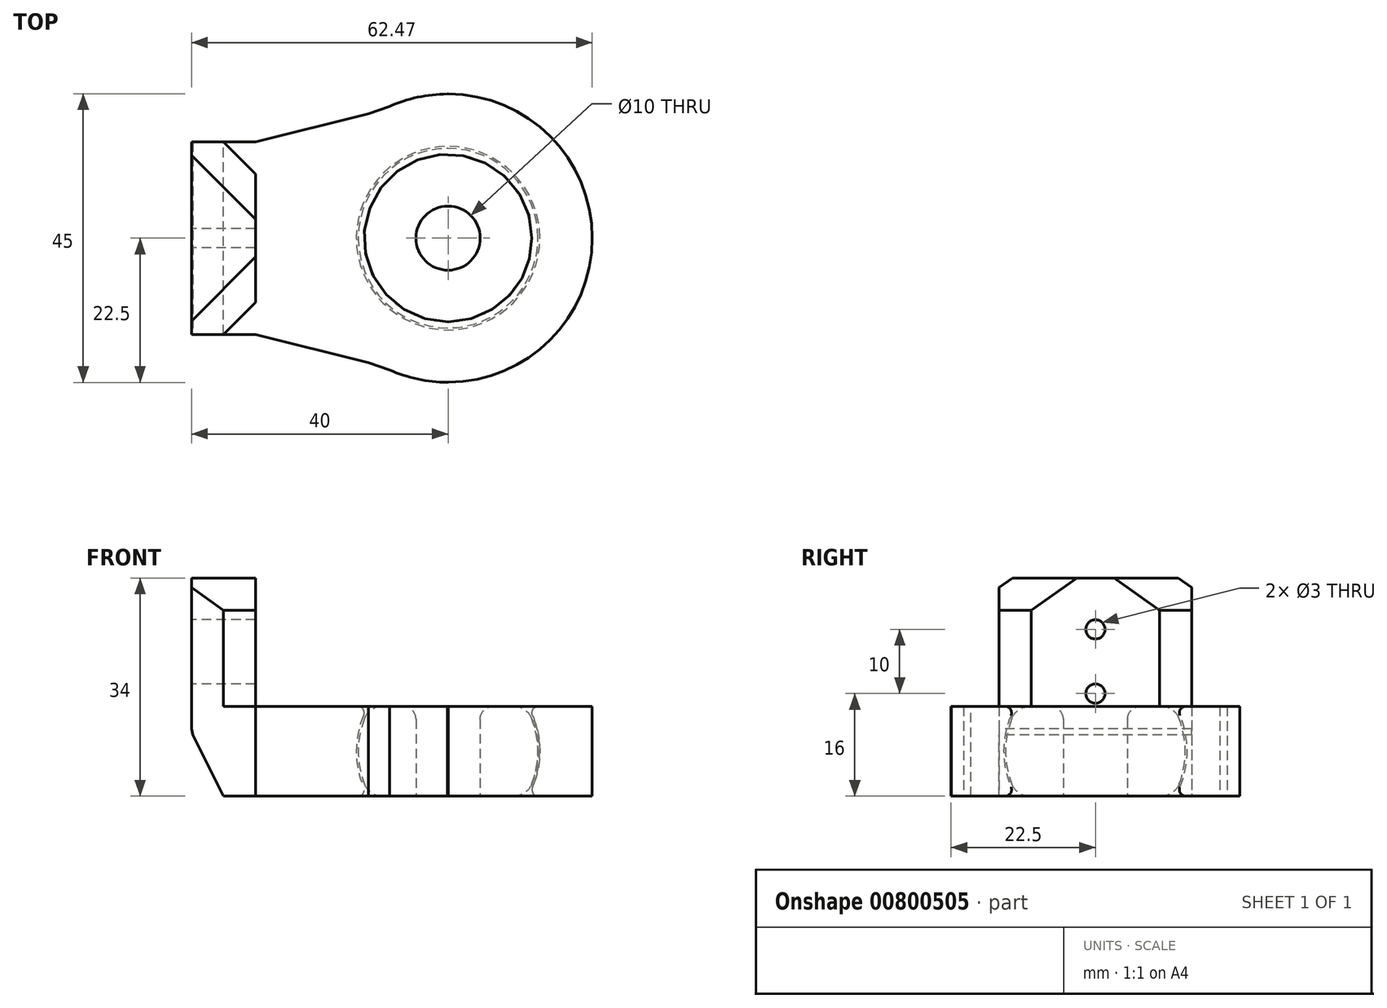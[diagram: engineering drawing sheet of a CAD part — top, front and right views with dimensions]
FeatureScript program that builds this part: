
annotation { "Feature Type Name" : "Feature", "Feature Type Description" : "" }
export const myFeature = defineFeature(function(context is Context, id is Id, definition is map)
    precondition{}
    {
        {
            var Q0;
            Q0=qCreatedBy(makeId("Front.planeOp"),FACE);
            var sketch = newSketch(context, id + "F0", { "sketchPlane" : qUnion([Q0])});
            skArc(sketch, "E0", {"start": v(12.12, 0) * mm, "mid": v(14, 7) * mm, "end": v(12.12, 14) * mm});
            skLineSegment(sketch, "E1", {"start": v(5, 14) * mm, "end": v(12.12, 14) * mm});
            skLineSegment(sketch, "E2", {"start": v(5, 0) * mm, "end": v(12.12, 0) * mm});
            skLineSegment(sketch, "E3", {"start": v(5, 0) * mm, "end": v(5, 14) * mm});
            skPoint(sketch, "E4.start.orphan", {"position": v(0, 0) * mm});
            skArc(sketch, "E5", {"start": v(12.47, 0) * mm, "mid": v(14.3, 7) * mm, "end": v(12.47, 14) * mm});
            skLineSegment(sketch, "E6", {"start": v(12.47, 14) * mm, "end": v(22.47, 14) * mm});
            skLineSegment(sketch, "E7", {"start": v(12.47, 0) * mm, "end": v(22.47, 0) * mm});
            skLineSegment(sketch, "E8", {"start": v(22.47, 14) * mm, "end": v(22.47, 0) * mm});
            skSolve(sketch);
        }
        {
            var Q0;
            Q0=qCreatedBy(makeId("Front.planeOp"),FACE);
            var sketch = newSketch(context, id + "F1", { "sketchPlane" : qUnion([Q0])});
            skLineSegment(sketch, "E9", {"start": v(0, 0) * mm, "end": v(0, 25.21) * mm});
            skSolve(sketch);
        }
        {
            var Q0;
            Q0=makeQuery(id+"F0.imprint","IMPRINT",FACE,{"disambiguationData":[TD([[makeQuery(id+"F0.imprint","IMPRINT",EDGE,{"derivedFrom":sQuery(id+"F0.wireOp",EDGE,"E0")}),1.0]])]});
            var Q1;
            Q1=makeQuery(id+"F0.imprint","IMPRINT",FACE,{"disambiguationData":[TD([[makeQuery(id+"F0.imprint","IMPRINT",EDGE,{"derivedFrom":sQuery(id+"F0.wireOp",EDGE,"E5")}),-1.0]])]});
            var Q2;
            Q2=sQuery(id+"F1.wireOp",EDGE,"E9");
            revolve(context, id + "F2", {"surfaceOperationType" : NewSurfaceOperationType.NEW, "entities" : qUnion([Q0, Q1]), "axis" : qUnion([Q2]), "revolveType" : RevolveType.FULL});
        }
        {
            var Q0;
            Q0=makeQuery(id+"F2.opRevolve","SWEPT_EDGE",EDGE,{"disambiguationData":[OSD([sQuery(id+"F0.wireOp",EDGE,"E0"),sQuery(id+"F0.wireOp",EDGE,"E1")])]});
            var Q1;
            Q1=makeQuery(id+"F2.opRevolve","SWEPT_EDGE",EDGE,{"disambiguationData":[OSD([sQuery(id+"F0.wireOp",EDGE,"E0"),sQuery(id+"F0.wireOp",EDGE,"E2")])]});
            fillet(context, id + "F3", {"entities" : qUnion([Q0, Q1]), "radius" : 3 * mm, "tangentPropagation" : true, "allowEdgeOverflow" : false});
        }
        {
            var Q0;
            Q0=makeQuery(id+"F2.opRevolve","SWEPT_EDGE",EDGE,{"disambiguationData":[OSD([sQuery(id+"F0.wireOp",EDGE,"E5"),sQuery(id+"F0.wireOp",EDGE,"E6")])]});
            var Q1;
            Q1=makeQuery(id+"F2.opRevolve","SWEPT_EDGE",EDGE,{"disambiguationData":[OSD([sQuery(id+"F0.wireOp",EDGE,"E5"),sQuery(id+"F0.wireOp",EDGE,"E7")])]});
            fillet(context, id + "F4", {"entities" : qUnion([Q0, Q1]), "radius" : 1 * mm, "tangentPropagation" : true, "allowEdgeOverflow" : false});
        }
        {
            var Q0;
            Q0=qCreatedBy(makeId("Top.planeOp"),FACE);
            var sketch = newSketch(context, id + "F5", { "sketchPlane" : qUnion([Q0])});
            skLineSegment(sketch, "E10", {"start": v(0, 19.22) * mm, "end": v(-15.75, 9.08) * mm});
            skLineSegment(sketch, "E11", {"start": v(-15.75, 9.08) * mm, "end": v(-15.75, -9.32) * mm});
            skLineSegment(sketch, "E12", {"start": v(-15.75, -9.32) * mm, "end": v(0, -18.87) * mm});
            skLineSegment(sketch, "E13", {"start": v(0, -18.87) * mm, "end": v(0, -22.5) * mm});
            skLineSegment(sketch, "E14", {"start": v(0, 22.5) * mm, "end": v(0, 19.22) * mm});
            skLineSegment(sketch, "E15", {"start": v(0, -22.5) * mm, "end": v(-30, -15) * mm});
            skLineSegment(sketch, "E16", {"start": v(-30, -15) * mm, "end": v(-30, 15) * mm});
            skLineSegment(sketch, "E17", {"start": v(-30, 15) * mm, "end": v(0, 22.5) * mm});
            skSolve(sketch);
        }
        {
            var Q0;
            Q0=qSketchRegion(id+"F5",true);
            extrude(context, id + "F6", {"entities" : qUnion([Q0]), "operationType" : NewBodyOperationType.ADD, "depth" : 14 * mm, "offsetDistance" : 25 * mm});
        }
        {
            var Q0;
            Q0=makeQuery(id+"F6.boolean.opBoolean","INTERSECT",EDGE,{"disambiguationData":[OD(1.0)],"derivedFrom":[makeQuery(id+"F2.opRevolve","SWEPT_FACE",FACE,{"disambiguationData":[OSD([sQuery(id+"F0.wireOp",EDGE,"E8")])]}),makeQuery(id+"F6.opExtrude","SWEPT_FACE",FACE,{"disambiguationData":[OSD([sQuery(id+"F5.wireOp",EDGE,"E15")])]})]});
            var Q1;
            Q1=makeQuery(id+"F6.boolean.opBoolean","INTERSECT",EDGE,{"disambiguationData":[OD(1.0)],"derivedFrom":[makeQuery(id+"F2.opRevolve","SWEPT_FACE",FACE,{"disambiguationData":[OSD([sQuery(id+"F0.wireOp",EDGE,"E8")])]}),makeQuery(id+"F6.opExtrude","SWEPT_FACE",FACE,{"disambiguationData":[OSD([sQuery(id+"F5.wireOp",EDGE,"E17")])]})]});
            chamfer(context, id + "F7", {"entities" : qUnion([Q0, Q1]), "width" : 20 * mm, "tangentPropagation" : true});
        }
        {
            var Q0;
            Q0=makeQuery(id+"F6.opExtrude","SWEPT_FACE",FACE,{"disambiguationData":[OSD([sQuery(id+"F5.wireOp",EDGE,"E16")])]});
            extrude(context, id + "F8", {"entities" : qUnion([Q0]), "operationType" : NewBodyOperationType.ADD, "depth" : 10 * mm, "offsetDistance" : 25 * mm});
        }
        {
            var Q0;
            {var subQ0=sQuery(id+"F5.wireOp",EDGE,"E16");Q0=makeQuery(id+"F8.boolean.opBoolean","MERGE",FACE,{"derivedFrom":[makeQuery(id+"F6.boolean.opBoolean","MERGE",FACE,{"derivedFrom":[makeQuery(id+"F2.opRevolve","SWEPT_FACE",FACE,{"disambiguationData":[OSD([sQuery(id+"F0.wireOp",EDGE,"E6")])]}),makeQuery(id+"F6.opExtrude","CAP_FACE",FACE,{"disambiguationData":[OSD([sQuery(id+"F5.wireOp",EDGE,"E10"),sQuery(id+"F5.wireOp",EDGE,"E11"),sQuery(id+"F5.wireOp",EDGE,"E12"),sQuery(id+"F5.wireOp",EDGE,"E13"),sQuery(id+"F5.wireOp",EDGE,"E14"),sQuery(id+"F5.wireOp",EDGE,"E15"),subQ0,sQuery(id+"F5.wireOp",EDGE,"E17")])],"isStart":false})]}),makeQuery(id+"F8.opExtrude","SWEPT_FACE",FACE,{"disambiguationData":[OSD([subQ0]),TDD([makeQuery(id+"F6.opExtrude","CAP_EDGE",EDGE,{"disambiguationData":[OSD([subQ0])],"isStart":false})])]})]});}
            extrude(context, id + "F9", {"entities" : qUnion([Q0]), "operationType" : NewBodyOperationType.ADD, "depth" : 10 * mm, "offsetDistance" : 25 * mm});
        }
        {
            var Q0;
            Q0=qCreatedBy(makeId("Front.planeOp"),FACE);
            var sketch = newSketch(context, id + "F10", { "sketchPlane" : qUnion([Q0])});
            skLineSegment(sketch, "E18", {"start": v(27.5, 14) * mm, "end": v(-22.5, 14) * mm});
            skLineSegment(sketch, "E19", {"start": v(-22.5, 14) * mm, "end": v(-22.5, 114) * mm});
            skLineSegment(sketch, "E20", {"start": v(-22.5, 114) * mm, "end": v(27.5, 114) * mm});
            skLineSegment(sketch, "E21", {"start": v(27.5, 114) * mm, "end": v(27.5, 14) * mm});
            skSolve(sketch);
        }
        {
            var Q0;
            Q0=makeQuery(id+"F10.imprint","IMPRINT",FACE,{"disambiguationData":[TD([[makeQuery(id+"F10.imprint","IMPRINT",EDGE,{"derivedFrom":sQuery(id+"F10.wireOp",EDGE,"E18")}),-1.0]])]});
            extrude(context, id + "F11", {"entities" : qUnion([Q0]), "operationType" : NewBodyOperationType.REMOVE, "endBound" : BoundingType.SYMMETRIC, "oppositeDirection" : true, "depth" : 100 * mm, "offsetDistance" : 25 * mm});
        }
        {
            var Q0;
            Q0=makeQuery(id+"F9.opExtrude","CAP_FACE",FACE,{"disambiguationData":[OSD([sQuery(id+"F0.wireOp",EDGE,"E6"),sQuery(id+"F5.wireOp",EDGE,"E10"),sQuery(id+"F5.wireOp",EDGE,"E11"),sQuery(id+"F5.wireOp",EDGE,"E12"),sQuery(id+"F5.wireOp",EDGE,"E13"),sQuery(id+"F5.wireOp",EDGE,"E14"),sQuery(id+"F5.wireOp",EDGE,"E15"),sQuery(id+"F5.wireOp",EDGE,"E16"),sQuery(id+"F5.wireOp",EDGE,"E17")])],"isStart":false});
            extrude(context, id + "F12", {"entities" : qUnion([Q0]), "operationType" : NewBodyOperationType.ADD, "depth" : 10 * mm, "offsetDistance" : 25 * mm});
        }
        {
            var Q0;
            {var subQ0=sQuery(id+"F5.wireOp",EDGE,"E16");Q0=makeQuery(id+"F12.boolean.opBoolean","MERGE",FACE,{"derivedFrom":[makeQuery(id+"F9.boolean.opBoolean","MERGE",FACE,{"derivedFrom":[makeQuery(id+"F8.opExtrude","CAP_FACE",FACE,{"disambiguationData":[OSD([subQ0])],"isStart":false}),makeQuery(id+"F9.opExtrude","SWEPT_FACE",FACE,{"disambiguationData":[OSD([subQ0])]})]}),makeQuery(id+"F12.opExtrude","SWEPT_FACE",FACE,{"disambiguationData":[OSD([subQ0])]})]});}
            var sketch = newSketch(context, id + "F13", { "sketchPlane" : qUnion([Q0])});
            skCircle(sketch, "E22", {"center": v(0, 16) * mm, "radius": 1.5 * mm});
            skCircle(sketch, "E23", {"center": v(0, 26) * mm, "radius": 1.5 * mm});
            skSolve(sketch);
        }
        {
            var Q0;
            Q0=qSketchRegion(id+"F13",true);
            extrude(context, id + "F14", {"entities" : qUnion([Q0]), "operationType" : NewBodyOperationType.REMOVE, "oppositeDirection" : true, "depth" : 25 * mm, "offsetDistance" : 25 * mm});
        }
        {
            var Q0;
            Q0=makeQuery(id+"F2.opRevolve","SWEPT_EDGE",EDGE,{"disambiguationData":[OSD([sQuery(id+"F0.wireOp",EDGE,"E1"),sQuery(id+"F0.wireOp",EDGE,"E3")])]});
            fillet(context, id + "F15", {"entities" : qUnion([Q0]), "radius" : 2 * mm, "tangentPropagation" : true, "allowEdgeOverflow" : false});
        }
        {
            var Q0;
            {var subQ0=sQuery(id+"F10.wireOp",EDGE,"E19");Q0=makeQuery(id+"F12.boolean.opBoolean","MERGE",FACE,{"derivedFrom":[makeQuery(id+"F11.boolean.opBoolean","COPY",FACE,{"derivedFrom":makeQuery(id+"F11.opExtrude","SWEPT_FACE",FACE,{"disambiguationData":[OSD([subQ0])]})}),makeQuery(id+"F12.opExtrude","SWEPT_FACE",FACE,{"disambiguationData":[OSD([sQuery(id+"F0.wireOp",EDGE,"E6"),sQuery(id+"F5.wireOp",EDGE,"E10"),sQuery(id+"F5.wireOp",EDGE,"E11"),sQuery(id+"F5.wireOp",EDGE,"E12"),sQuery(id+"F5.wireOp",EDGE,"E13"),sQuery(id+"F5.wireOp",EDGE,"E14"),sQuery(id+"F5.wireOp",EDGE,"E15"),sQuery(id+"F5.wireOp",EDGE,"E16"),sQuery(id+"F5.wireOp",EDGE,"E17"),subQ0])]})]});}
            extrude(context, id + "F16", {"entities" : qUnion([Q0]), "operationType" : NewBodyOperationType.REMOVE, "oppositeDirection" : true, "depth" : 7.5 * mm, "offsetDistance" : 25 * mm});
        }
        {
            var Q0;
            {var subQ0=sQuery(id+"F5.wireOp",EDGE,"E16");Q0=makeQuery(id+"F8.opExtrude","CAP_EDGE",EDGE,{"disambiguationData":[OSD([subQ0]),TDD([makeQuery(id+"F6.opExtrude","CAP_EDGE",EDGE,{"disambiguationData":[OSD([subQ0])],"isStart":true})])],"isStart":false});}
            chamfer(context, id + "F17", {"entities" : qUnion([Q0]), "chamferType" : ChamferType.TWO_OFFSETS, "width1" : 5 * mm, "oppositeDirection" : false, "width2" : 10 * mm, "tangentPropagation" : true});
        }
        {
            var Q0;
            {var subQ0=sQuery(id+"F5.wireOp",EDGE,"E16");Q0=makeQuery(id+"F17.opChamfer","BLEND_EDGE",EDGE,{"blendedFrom":[makeQuery(id+"F8.opExtrude","CAP_EDGE",EDGE,{"disambiguationData":[OSD([subQ0]),TDD([makeQuery(id+"F6.opExtrude","CAP_EDGE",EDGE,{"disambiguationData":[OSD([subQ0])],"isStart":true})])],"isStart":false}),makeQuery(id+"F12.boolean.opBoolean","MERGE",FACE,{"derivedFrom":[makeQuery(id+"F9.boolean.opBoolean","MERGE",FACE,{"derivedFrom":[makeQuery(id+"F8.opExtrude","CAP_FACE",FACE,{"disambiguationData":[OSD([subQ0])],"isStart":false}),makeQuery(id+"F9.opExtrude","SWEPT_FACE",FACE,{"disambiguationData":[OSD([subQ0])]})]}),makeQuery(id+"F12.opExtrude","SWEPT_FACE",FACE,{"disambiguationData":[OSD([subQ0])]})]})],"blendedInto":[makeQuery(id+"F12.boolean.opBoolean","MERGE",FACE,{"derivedFrom":[makeQuery(id+"F9.boolean.opBoolean","MERGE",FACE,{"derivedFrom":[makeQuery(id+"F8.opExtrude","CAP_FACE",FACE,{"disambiguationData":[OSD([subQ0])],"isStart":false}),makeQuery(id+"F9.opExtrude","SWEPT_FACE",FACE,{"disambiguationData":[OSD([subQ0])]})]}),makeQuery(id+"F12.opExtrude","SWEPT_FACE",FACE,{"disambiguationData":[OSD([subQ0])]})]})]});}
            chamfer(context, id + "F18", {"entities" : qUnion([Q0]), "width" : 2 * mm, "tangentPropagation" : true});
        }
        {
            var Q0;
            {var subQ0=sQuery(id+"F5.wireOp",EDGE,"E17");var subQ1=sQuery(id+"F5.wireOp",EDGE,"E16");Q0=makeQuery(id+"F16.boolean.opBoolean","INTERSECT",EDGE,{"derivedFrom":[makeQuery(id+"F12.boolean.opBoolean","MERGE",FACE,{"derivedFrom":[makeQuery(id+"F9.boolean.opBoolean","MERGE",FACE,{"derivedFrom":[makeQuery(id+"F8.opExtrude","SWEPT_FACE",FACE,{"disambiguationData":[OSD([subQ1,subQ0])]}),makeQuery(id+"F9.opExtrude","SWEPT_FACE",FACE,{"disambiguationData":[OSD([subQ1,subQ0])]})]}),makeQuery(id+"F12.opExtrude","SWEPT_FACE",FACE,{"disambiguationData":[OSD([subQ1,subQ0])]})]}),makeQuery(id+"F16.opExtrude","CAP_FACE",FACE,{"disambiguationData":[OSD([sQuery(id+"F0.wireOp",EDGE,"E6"),sQuery(id+"F5.wireOp",EDGE,"E10"),sQuery(id+"F5.wireOp",EDGE,"E11"),sQuery(id+"F5.wireOp",EDGE,"E12"),sQuery(id+"F5.wireOp",EDGE,"E13"),sQuery(id+"F5.wireOp",EDGE,"E14"),sQuery(id+"F5.wireOp",EDGE,"E15"),subQ1,subQ0,sQuery(id+"F10.wireOp",EDGE,"E19")])],"isStart":false})]});}
            var Q1;
            {var subQ0=sQuery(id+"F5.wireOp",EDGE,"E16");var subQ1=sQuery(id+"F5.wireOp",EDGE,"E15");Q1=makeQuery(id+"F16.boolean.opBoolean","INTERSECT",EDGE,{"derivedFrom":[makeQuery(id+"F12.boolean.opBoolean","MERGE",FACE,{"derivedFrom":[makeQuery(id+"F9.boolean.opBoolean","MERGE",FACE,{"derivedFrom":[makeQuery(id+"F8.opExtrude","SWEPT_FACE",FACE,{"disambiguationData":[OSD([subQ1,subQ0])]}),makeQuery(id+"F9.opExtrude","SWEPT_FACE",FACE,{"disambiguationData":[OSD([subQ1,subQ0])]})]}),makeQuery(id+"F12.opExtrude","SWEPT_FACE",FACE,{"disambiguationData":[OSD([subQ1,subQ0])]})]}),makeQuery(id+"F16.opExtrude","CAP_FACE",FACE,{"disambiguationData":[OSD([sQuery(id+"F0.wireOp",EDGE,"E6"),sQuery(id+"F5.wireOp",EDGE,"E10"),sQuery(id+"F5.wireOp",EDGE,"E11"),sQuery(id+"F5.wireOp",EDGE,"E12"),sQuery(id+"F5.wireOp",EDGE,"E13"),sQuery(id+"F5.wireOp",EDGE,"E14"),subQ1,subQ0,sQuery(id+"F5.wireOp",EDGE,"E17"),sQuery(id+"F10.wireOp",EDGE,"E19")])],"isStart":false})]});}
            chamfer(context, id + "F19", {"entities" : qUnion([Q0, Q1]), "width" : 5 * mm, "tangentPropagation" : true});
        }
        {
            var Q0;
            {var subQ0=sQuery(id+"F5.wireOp",EDGE,"E17");var subQ1=sQuery(id+"F5.wireOp",EDGE,"E16");var subQ2=sQuery(id+"F5.wireOp",EDGE,"E15");var subQ3=sQuery(id+"F5.wireOp",EDGE,"E14");var subQ4=sQuery(id+"F5.wireOp",EDGE,"E13");var subQ5=sQuery(id+"F5.wireOp",EDGE,"E12");var subQ6=sQuery(id+"F5.wireOp",EDGE,"E11");var subQ7=sQuery(id+"F5.wireOp",EDGE,"E10");var subQ8=sQuery(id+"F0.wireOp",EDGE,"E6");Q0=makeQuery(id+"F19.opChamfer","BLEND_EDGE",EDGE,{"blendedFrom":[makeQuery(id+"F16.boolean.opBoolean","INTERSECT",EDGE,{"derivedFrom":[makeQuery(id+"F12.boolean.opBoolean","MERGE",FACE,{"derivedFrom":[makeQuery(id+"F9.boolean.opBoolean","MERGE",FACE,{"derivedFrom":[makeQuery(id+"F8.opExtrude","SWEPT_FACE",FACE,{"disambiguationData":[OSD([subQ1,subQ0])]}),makeQuery(id+"F9.opExtrude","SWEPT_FACE",FACE,{"disambiguationData":[OSD([subQ1,subQ0])]})]}),makeQuery(id+"F12.opExtrude","SWEPT_FACE",FACE,{"disambiguationData":[OSD([subQ1,subQ0])]})]}),makeQuery(id+"F16.opExtrude","CAP_FACE",FACE,{"disambiguationData":[OSD([subQ8,subQ7,subQ6,subQ5,subQ4,subQ3,subQ2,subQ1,subQ0,sQuery(id+"F10.wireOp",EDGE,"E19")])],"isStart":false})]}),makeQuery(id+"F12.opExtrude","CAP_FACE",FACE,{"disambiguationData":[OSD([subQ8,subQ7,subQ6,subQ5,subQ4,subQ3,subQ2,subQ1,subQ0])],"isStart":false})],"blendedInto":[makeQuery(id+"F12.opExtrude","CAP_FACE",FACE,{"disambiguationData":[OSD([subQ8,subQ7,subQ6,subQ5,subQ4,subQ3,subQ2,subQ1,subQ0])],"isStart":false})]});}
            var Q1;
            {var subQ0=sQuery(id+"F5.wireOp",EDGE,"E17");var subQ1=sQuery(id+"F5.wireOp",EDGE,"E16");var subQ2=sQuery(id+"F5.wireOp",EDGE,"E15");var subQ3=sQuery(id+"F5.wireOp",EDGE,"E14");var subQ4=sQuery(id+"F5.wireOp",EDGE,"E13");var subQ5=sQuery(id+"F5.wireOp",EDGE,"E12");var subQ6=sQuery(id+"F5.wireOp",EDGE,"E11");var subQ7=sQuery(id+"F5.wireOp",EDGE,"E10");var subQ8=sQuery(id+"F0.wireOp",EDGE,"E6");Q1=makeQuery(id+"F19.opChamfer","BLEND_EDGE",EDGE,{"blendedFrom":[makeQuery(id+"F16.boolean.opBoolean","INTERSECT",EDGE,{"derivedFrom":[makeQuery(id+"F12.boolean.opBoolean","MERGE",FACE,{"derivedFrom":[makeQuery(id+"F9.boolean.opBoolean","MERGE",FACE,{"derivedFrom":[makeQuery(id+"F8.opExtrude","SWEPT_FACE",FACE,{"disambiguationData":[OSD([subQ2,subQ1])]}),makeQuery(id+"F9.opExtrude","SWEPT_FACE",FACE,{"disambiguationData":[OSD([subQ2,subQ1])]})]}),makeQuery(id+"F12.opExtrude","SWEPT_FACE",FACE,{"disambiguationData":[OSD([subQ2,subQ1])]})]}),makeQuery(id+"F16.opExtrude","CAP_FACE",FACE,{"disambiguationData":[OSD([subQ8,subQ7,subQ6,subQ5,subQ4,subQ3,subQ2,subQ1,subQ0,sQuery(id+"F10.wireOp",EDGE,"E19")])],"isStart":false})]}),makeQuery(id+"F12.opExtrude","CAP_FACE",FACE,{"disambiguationData":[OSD([subQ8,subQ7,subQ6,subQ5,subQ4,subQ3,subQ2,subQ1,subQ0])],"isStart":false})],"blendedInto":[makeQuery(id+"F12.opExtrude","CAP_FACE",FACE,{"disambiguationData":[OSD([subQ8,subQ7,subQ6,subQ5,subQ4,subQ3,subQ2,subQ1,subQ0])],"isStart":false})]});}
            chamfer(context, id + "F20", {"entities" : qUnion([Q0, Q1]), "width" : 5 * mm, "tangentPropagation" : true});
        }
    });
